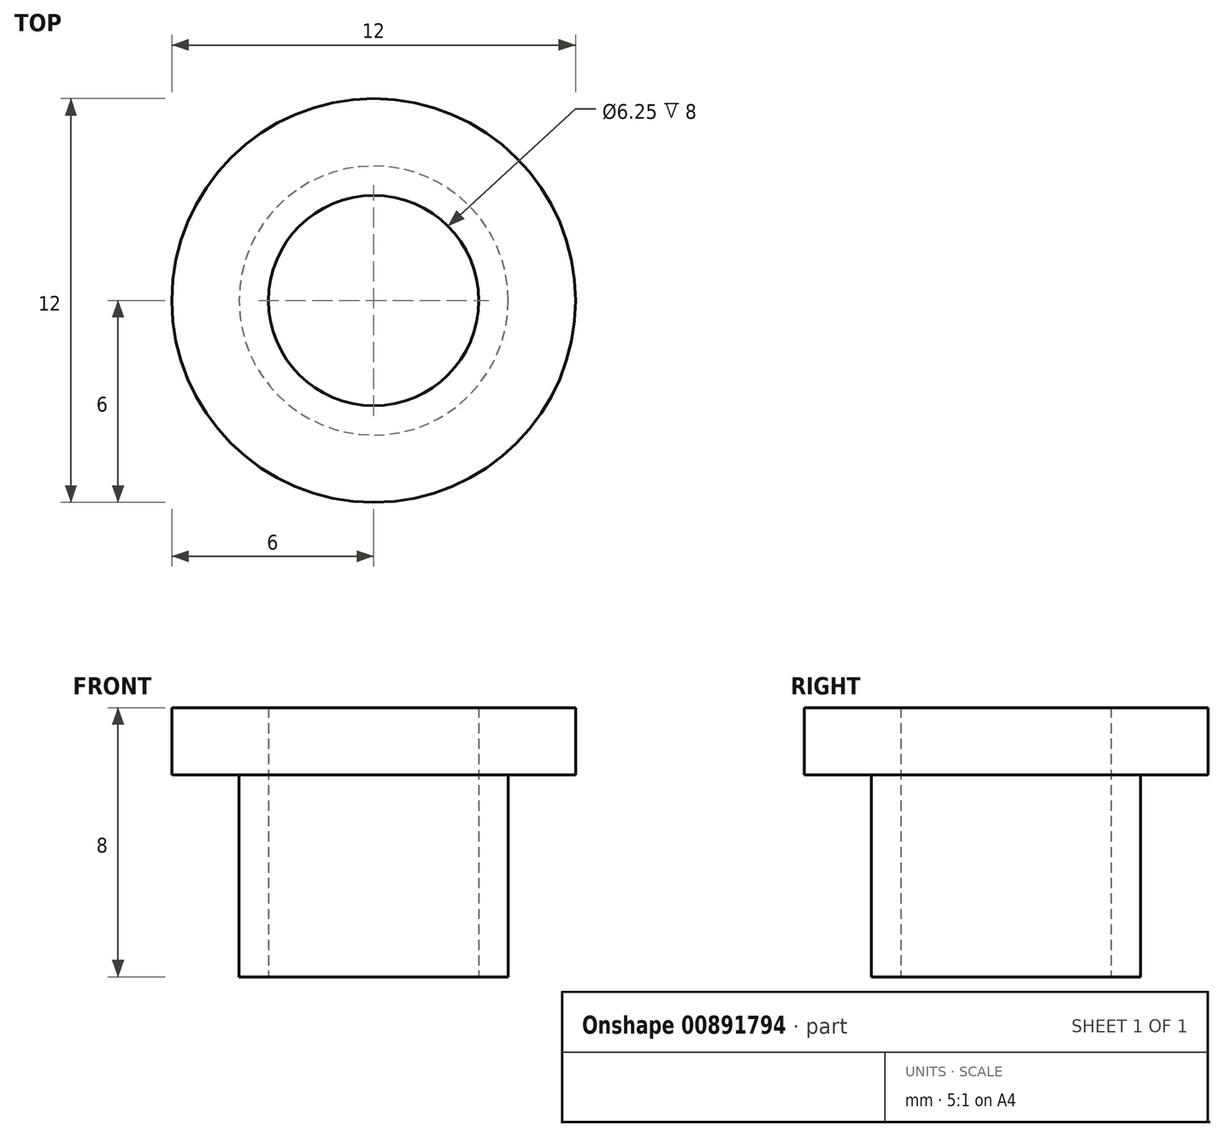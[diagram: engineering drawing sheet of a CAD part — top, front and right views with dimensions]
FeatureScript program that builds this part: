
annotation { "Feature Type Name" : "Feature", "Feature Type Description" : "" }
export const myFeature = defineFeature(function(context is Context, id is Id, definition is map)
    precondition{}
    {
        {
            var Q0;
            Q0=qCreatedBy(makeId("Top.planeOp"),FACE);
            var sketch = newSketch(context, id + "F0", { "sketchPlane" : qUnion([Q0])});
            skCircle(sketch, "E0", {"center": v(0, 0) * mm, "radius": 4 * mm});
            skCircle(sketch, "E1", {"center": v(0, 0) * mm, "radius": 3.12 * mm});
            skSolve(sketch);
        }
        {
            var Q0;
            Q0=makeQuery(id+"F0.imprint","IMPRINT",FACE,{"disambiguationData":[TD([[makeQuery(id+"F0.imprint","IMPRINT",EDGE,{"derivedFrom":sQuery(id+"F0.wireOp",EDGE,"E0")}),1.0]])]});
            extrude(context, id + "F1", {"entities" : qUnion([Q0]), "endBound" : BoundingType.SYMMETRIC, "depth" : 8 * mm, "offsetDistance" : 25.4 * mm});
        }
        {
            var Q0;
            Q0=makeQuery(id+"F1.opExtrude","CAP_FACE",FACE,{"disambiguationData":[OSD([sQuery(id+"F0.wireOp",EDGE,"E0"),sQuery(id+"F0.wireOp",EDGE,"E1")])],"isStart":false});
            var sketch = newSketch(context, id + "F2", { "sketchPlane" : qUnion([Q0])});
            skCircle(sketch, "E2", {"center": v(0, 0) * mm, "radius": 3.95 * mm});
            skCircle(sketch, "E3", {"center": v(0, 0) * mm, "radius": 6 * mm});
            skSolve(sketch);
        }
        {
            var Q0;
            Q0=makeQuery(id+"F2.imprint","IMPRINT",FACE,{"disambiguationData":[TD([[makeQuery(id+"F2.imprint","IMPRINT",EDGE,{"derivedFrom":sQuery(id+"F2.wireOp",EDGE,"E3")}),1.0]])]});
            extrude(context, id + "F3", {"entities" : qUnion([Q0]), "operationType" : NewBodyOperationType.ADD, "oppositeDirection" : true, "depth" : 2 * mm, "offsetDistance" : 25.4 * mm});
        }
    });
